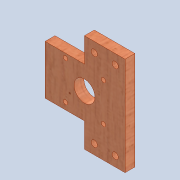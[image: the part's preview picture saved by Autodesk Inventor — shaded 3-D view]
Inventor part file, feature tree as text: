
AUTODESK INVENTOR PART (.ipt)
format: ipt  version: 2020 (Build 240168000, 168)  size: 266,752 bytes
history: native  units: mm
features: sketch x4, extrude x3, hole x1, pattern_linear x1
ambient origin geometry x8: Origin, YZ Plane, XZ Plane, XY Plane, X Axis, Y Axis, Z Axis, Center Point
bodies: Solid1 (feature_tree)
feature tree (9):
  extrude  "Extrusion1"  Depth=40.0mm
  extrude  "Extrusion5"  Depth=20.0mm
  extrude  "Extrusion6"  Depth=33.0mm
  hole  "Hole1"  [1 undecoded]
  pattern_linear  "Rectangular Pattern1"  Spacing1=33.0mm  [1 undecoded]
  sketch  "Sketch1"  dims[d0=65.0mm d1=40.0mm]
  sketch  "Sketch5"  dims[d2=8.0mm d3=0.0mm d22=20.0mm]
  sketch  "Sketch6"  dims[d23=20.0mm d24=33.0mm]
  sketch  "Sketch7"  dims[d25=10.0mm d26=0.0mm d29=31.0mm d30=33.0mm d31=39.0mm d32=3.5mm d33=17.0mm d34=10.0mm d35=0.0mm d36=8.0mm d37=8.0mm d38=8.0mm d39=17.0mm d40=8.0mm d41=64.0mm d42=5.0mm d43=6.0mm d44=4.0mm d45=2.0mm d46=90.0deg d47=8.0mm d48=20.594885mm d49=20.0mm d51=64.0mm d52=20.0mm d54=17.0mm]
note: 2 required parameter values undecoded (feature->parameter linkage not recoverable at this tier; creation-order binding heuristic only, values carry confidence <= 0.55)
